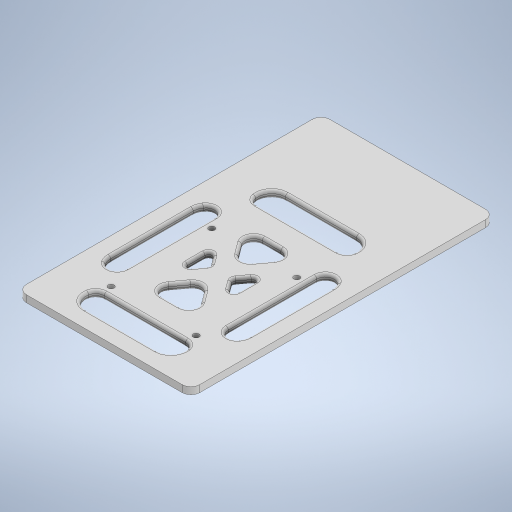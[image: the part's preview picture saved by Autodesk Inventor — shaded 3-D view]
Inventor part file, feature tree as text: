
AUTODESK INVENTOR PART (.ipt)
format: ipt  version: 2023 (Build 270158000, 158)  size: 573,952 bytes
history: native  units: in
note: dims shown in document units (in); Inventor stores cm internally (conversion verified against a paired STEP export)
features: fillet x6, sketch x3, extrude x2, hole x1, thicken_offset x1
ambient origin geometry x8: Origin, YZ Plane, XZ Plane, XY Plane, X Axis, Y Axis, Z Axis, Center Point
bodies: Solid1 (feature_tree)
feature tree (13):
  extrude  "Extrusion1"  Depth=3.937in
  hole  "Hole1"  [1 undecoded]
  extrude  "Extrusion3"  Depth=0.1378in
  thicken_offset  "Thicken1"
  fillet  "Fillet4"  Radius=0.1378in
  fillet  "Fillet5"  Radius=2.2835in
  fillet  "Fillet6"  Radius=0.1378in
  fillet  "Fillet7"  Radius=0.3937in
  fillet  "Fillet8"  Radius=0.1969in
  fillet  "Fillet9"  Radius=0.3937in
  sketch  "Sketch1"  dims[d0=5.315in d1=3.937in]
  sketch  "Sketch3"  dims[d2=0.1575in d3=0.0in d11=2.2047in]
  sketch  "Sketch4"  dims[d12=3.3465in d13=0.1378in d14=0.1378in d15=2.2835in d17=0.1378in d18=0.1339in d19=0.2362in d20=0.248in d21=0.0787in d22=90.0deg d23=0.315in d24=0.8108in d27=0.3937in d28=0.1969in d29=0.3937in d30=0.1969in d31=0.1969in d32=0.1969in d33=0.1969in d34=0.0in d35=0.0in d37=1.9291in d38=3.0709in d40=1.5748in d41=1.1811in d42=0.1969in d43=0.315in d44=0.1969in d45=0.0787in d46=0.1969in d47=0.0591in]
note: 1 required parameter value undecoded (feature->parameter linkage not recoverable at this tier; creation-order binding heuristic only, values carry confidence <= 0.55)
